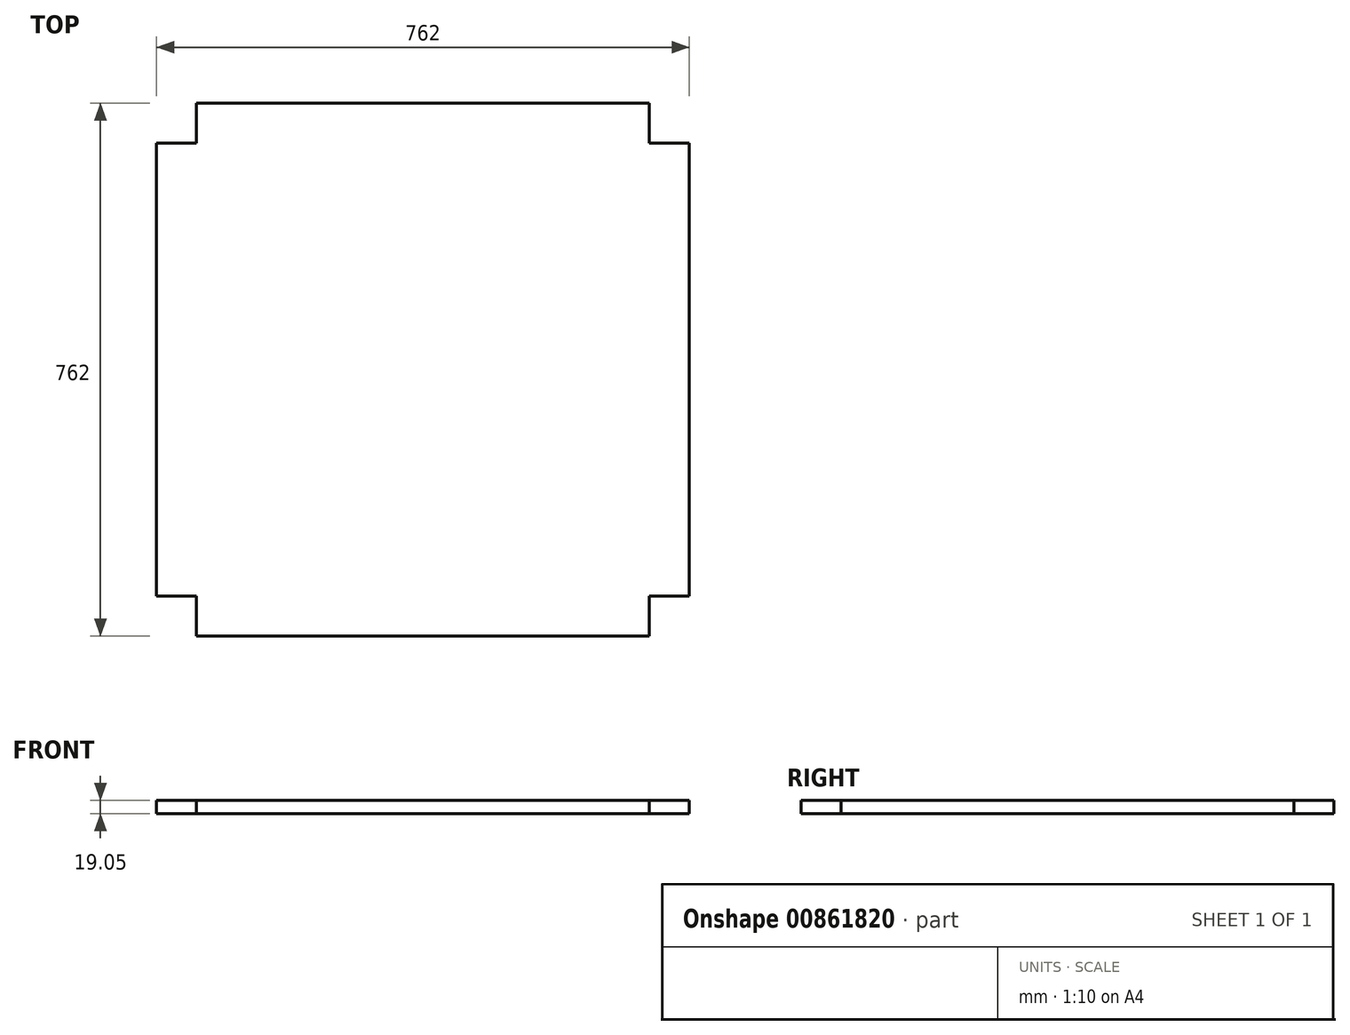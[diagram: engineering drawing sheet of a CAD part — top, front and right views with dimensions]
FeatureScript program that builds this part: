
annotation { "Feature Type Name" : "Feature", "Feature Type Description" : "" }
export const myFeature = defineFeature(function(context is Context, id is Id, definition is map)
    precondition{}
    {
        {
            var Q0;
            Q0=qCreatedBy(makeId("Top.planeOp"),FACE);
            var sketch = newSketch(context, id + "F0", { "sketchPlane" : qUnion([Q0])});
            skLineSegment(sketch, "E0.bottom", {"start": v(-344.18, 528.25) * mm, "end": v(417.82, 528.25) * mm});
            skLineSegment(sketch, "E0.top", {"start": v(-344.18, -233.75) * mm, "end": v(417.82, -233.75) * mm});
            skLineSegment(sketch, "E0.left", {"start": v(-344.18, 528.25) * mm, "end": v(-344.18, -233.75) * mm});
            skLineSegment(sketch, "E0.right", {"start": v(417.82, 528.25) * mm, "end": v(417.82, -233.75) * mm});
            skLineSegment(sketch, "E1", {"start": v(-287.03, 528.25) * mm, "end": v(-287.03, 471.1) * mm});
            skLineSegment(sketch, "E2", {"start": v(-287.03, 471.1) * mm, "end": v(-344.18, 471.1) * mm});
            skLineSegment(sketch, "E3", {"start": v(-344.18, -176.6) * mm, "end": v(-287.03, -176.6) * mm});
            skLineSegment(sketch, "E4", {"start": v(-287.03, -176.6) * mm, "end": v(-287.03, -233.75) * mm});
            skLineSegment(sketch, "E5", {"start": v(417.82, -176.6) * mm, "end": v(360.67, -176.6) * mm});
            skLineSegment(sketch, "E6", {"start": v(360.67, -176.6) * mm, "end": v(360.67, -233.75) * mm});
            skLineSegment(sketch, "E7", {"start": v(360.67, 528.25) * mm, "end": v(360.67, 471.1) * mm});
            skLineSegment(sketch, "E8", {"start": v(360.67, 471.1) * mm, "end": v(417.82, 471.1) * mm});
            skSolve(sketch);
        }
        {
            var Q0;
            {var subQ4=sQuery(id+"F0.wireOp",EDGE,"E1");Q0=makeQuery(id+"F0.imprint","IMPRINT",FACE,{"disambiguationData":[TD([[makeQuery(id+"F0.imprint","IMPRINT",EDGE,{"derivedFrom":subQ4}),1.0]])]});}
            extrude(context, id + "F1", {"entities" : qUnion([Q0]), "depth" : 19.05 * mm, "offsetDistance" : 25.4 * mm});
        }
    });
